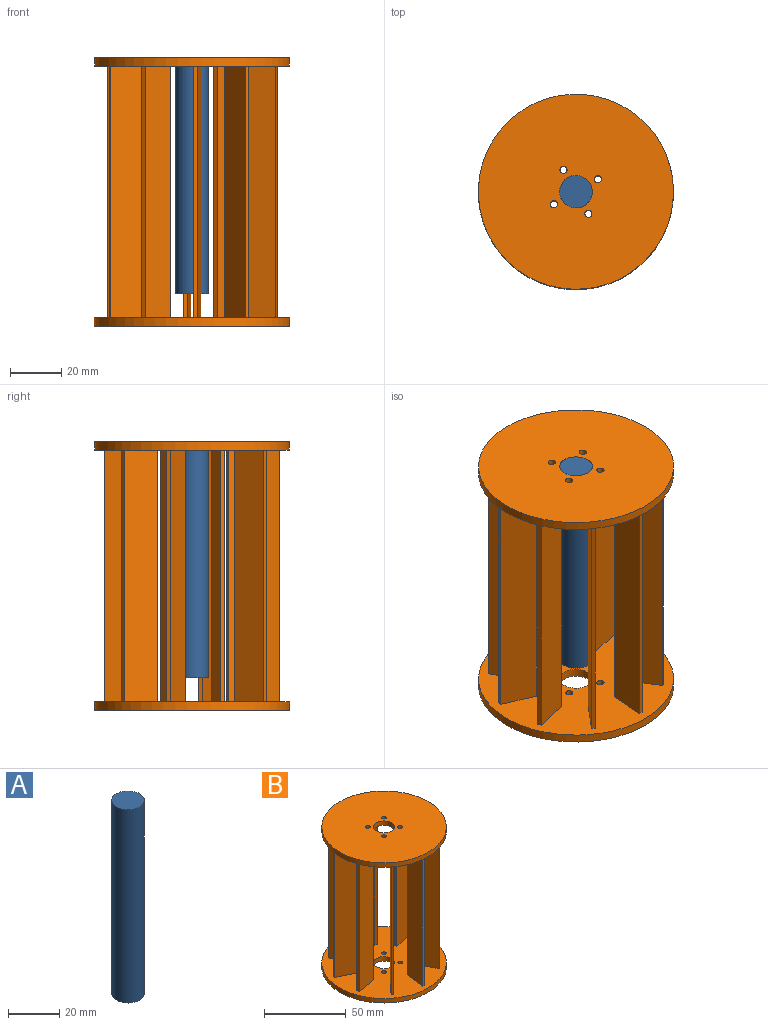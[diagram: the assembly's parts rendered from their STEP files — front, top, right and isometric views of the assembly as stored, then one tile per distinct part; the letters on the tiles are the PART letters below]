
ASSEMBLY  parts=2 mates=1
PART A: 3 faces, bbox 12.7x12.7x92.2 mm
  f0: cylinder r=6.35mm len=92.2mm, axis (0,0,-1), area 3678.7mm2, adj f1,f2
  f1: plane 12.7x12.7mm, normal (0,0,1), area 126.7mm2, adj f0
  f2: plane 12.7x12.7mm, normal (0,0,-1), area 126.7mm2, adj f0
PART B: 56 faces, bbox 76.2x76.2x104.9 mm
  f0: plane 76.2x76.2mm, normal (0,0,-1), area 4409.2mm2, adj f4,f51,f52,f53,f54,f55
  f1: plane 76.2x76.2mm, normal (0,0,1), area 4164mm2, adj f4,f5,f6,f7,f8,f9,f10,f11
  f2: plane 76.16x76.16mm, normal (0,0,-1), area 4159.5mm2, adj f5,f6,f7,f8,f9,f10,f11,f12
  f3: plane 76.16x76.16mm, normal (0,0,1), area 4404.7mm2, adj f45,f46,f47,f48,f49,f50
  f4: cylinder r=38.1mm len=76.2mm, axis (0,0,-1), area 790.5mm2, adj f0,f1
  f5: plane 98.3x15.03mm, normal (0.99,-0.11,0), area 1487.1mm2, adj f1,f2,f6,f8
  f6: plane 98.3x1.56mm, normal (0,1,0), area 153.3mm2, adj f1,f2,f5,f7
  f7: plane 98.3x15.03mm, normal (-0.99,0.12,0), area 1488.7mm2, adj f1,f2,f6,f8
  f8: plane 98.3x1.7mm, normal (0,-1,0), area 167.3mm2, adj f1,f2,f5,f7
  f9: plane 98.3x1.37mm, normal (-0.59,-0.81,0), area 167.3mm2, adj f1,f2,f10,f12
  f10: plane 98.3x11.14mm, normal (0.74,-0.68,0), area 1487.1mm2, adj f1,f2,f9,f11
  f11: plane 98.3x1.26mm, normal (0.59,0.81,0), area 153.3mm2, adj f1,f2,f10,f12
  f12: plane 98.3x11.06mm, normal (-0.73,0.68,0), area 1488.7mm2, adj f1,f2,f9,f11
  f13: plane 98.3x1.62mm, normal (-0.95,-0.31,0), area 167.3mm2, adj f1,f2,f14,f16
  f14: plane 98.3x14.83mm, normal (0.2,-0.98,0), area 1487.1mm2, adj f1,f2,f13,f15
  f15: plane 98.3x1.49mm, normal (0.95,0.31,0), area 153.3mm2, adj f1,f2,f14,f16
  f16: plane 98.3x14.88mm, normal (-0.19,0.98,0), area 1488.7mm2, adj f1,f2,f13,f15
  f17: plane 98.3x1.62mm, normal (-0.95,0.31,0), area 167.3mm2, adj f1,f2,f18,f20
  f18: plane 98.3x13.73mm, normal (-0.42,-0.91,0), area 1487.1mm2, adj f1,f2,f17,f19
  f19: plane 98.3x1.48mm, normal (0.95,-0.31,0), area 153.3mm2, adj f1,f2,f18,f20
  f20: plane 98.3x13.69mm, normal (0.43,0.9,0), area 1488.7mm2, adj f1,f2,f17,f19
  f21: plane 98.3x1.38mm, normal (-0.58,0.81,0), area 167.3mm2, adj f1,f2,f22,f24
  f22: plane 98.3x13.22mm, normal (-0.87,-0.49,0), area 1487.1mm2, adj f1,f2,f21,f23
  f23: plane 98.3x1.27mm, normal (0.58,-0.81,0), area 153.3mm2, adj f1,f2,f22,f24
  f24: plane 98.3x13.3mm, normal (0.88,0.48,0), area 1488.7mm2, adj f1,f2,f21,f23
  f25: plane 98.3x1.7mm, normal (0.01,1,0), area 167.3mm2, adj f1,f2,f26,f28
  f26: plane 98.3x15.01mm, normal (-0.99,0.12,0), area 1487.1mm2, adj f1,f2,f25,f27
  f27: plane 98.3x1.56mm, normal (-0.01,-1,0), area 153.3mm2, adj f1,f2,f26,f28
  f28: plane 98.3x15.01mm, normal (0.99,-0.13,0), area 1488.7mm2, adj f1,f2,f25,f27
  f29: plane 98.3x1.37mm, normal (0.6,0.8,0), area 167.3mm2, adj f1,f2,f30,f32
  f30: plane 98.3x11.04mm, normal (-0.73,0.68,0), area 1487.1mm2, adj f1,f2,f29,f31
  f31: plane 98.3x1.25mm, normal (-0.6,-0.8,0), area 153.3mm2, adj f1,f2,f30,f32
  f32: plane 98.3x10.96mm, normal (0.72,-0.69,0), area 1488.7mm2, adj f1,f2,f29,f31
  f33: plane 98.3x1.63mm, normal (0.96,0.3,0), area 167.3mm2, adj f1,f2,f34,f36
  f34: plane 98.3x14.86mm, normal (-0.19,0.98,0), area 1487.1mm2, adj f1,f2,f33,f35
  f35: plane 98.3x1.49mm, normal (-0.96,-0.3,0), area 153.3mm2, adj f1,f2,f34,f36
  f36: plane 98.3x14.9mm, normal (0.18,-0.98,0), area 1488.7mm2, adj f1,f2,f33,f35
  f37: plane 98.3x1.61mm, normal (0.95,-0.32,0), area 167.3mm2, adj f1,f2,f38,f40
  f38: plane 98.3x13.67mm, normal (0.43,0.9,0), area 1487.1mm2, adj f1,f2,f37,f39
  f39: plane 98.3x1.48mm, normal (-0.95,0.32,0), area 153.3mm2, adj f1,f2,f38,f40
  f40: plane 98.3x13.63mm, normal (-0.44,-0.9,0), area 1488.7mm2, adj f1,f2,f37,f39
  f41: plane 98.3x1.39mm, normal (0.57,-0.82,0), area 167.3mm2, adj f1,f2,f42,f44
  f42: plane 98.3x13.29mm, normal (0.88,0.48,0), area 1487.1mm2, adj f1,f2,f41,f43
  f43: plane 98.3x1.28mm, normal (-0.57,0.82,0), area 153.3mm2, adj f1,f2,f42,f44
  f44: plane 98.3x13.37mm, normal (-0.88,-0.47,0), area 1488.7mm2, adj f1,f2,f41,f43
  f45: cylinder r=38.08mm len=76.16mm, axis (0,0,-1), area 790.1mm2, adj f2,f3
  f46: cylinder r=1.4mm len=3.3mm, axis (0,0,-1), area 29mm2, adj f2,f3
  f47: cylinder r=1.4mm len=3.3mm, axis (0,0,-1), area 29mm2, adj f2,f3
  f48: cylinder r=6.35mm len=12.7mm, axis (0,0,-1), area 131.7mm2, adj f2,f3
  f49: cylinder r=1.4mm len=3.3mm, axis (0,0,-1), area 29mm2, adj f2,f3
  f50: cylinder r=1.4mm len=3.3mm, axis (0,0,-1), area 29mm2, adj f2,f3
  f51: cylinder r=1.4mm len=3.3mm, axis (0,0,-1), area 29mm2, adj f0,f1
  f52: cylinder r=1.4mm len=3.3mm, axis (0,0,-1), area 29mm2, adj f0,f1
  f53: cylinder r=6.35mm len=12.7mm, axis (0,0,-1), area 131.7mm2, adj f0,f1
  f54: cylinder r=1.4mm len=3.3mm, axis (0,0,-1), area 29mm2, adj f0,f1
  f55: cylinder r=1.4mm len=3.3mm, axis (0,0,-1), area 29mm2, adj f0,f1
PLACE A rot(axis=(0,0,-1),15.5deg) t=(23.03,76.9,25.41)mm fixed
PLACE B rot(axis=(0,0,-1),105.5deg) t=(23.03,76.9,12.71)mm
MATE revolute A.f0 <-> B.f4  axis (0,0,-1) through (23.03,76.9,117.61)mm
